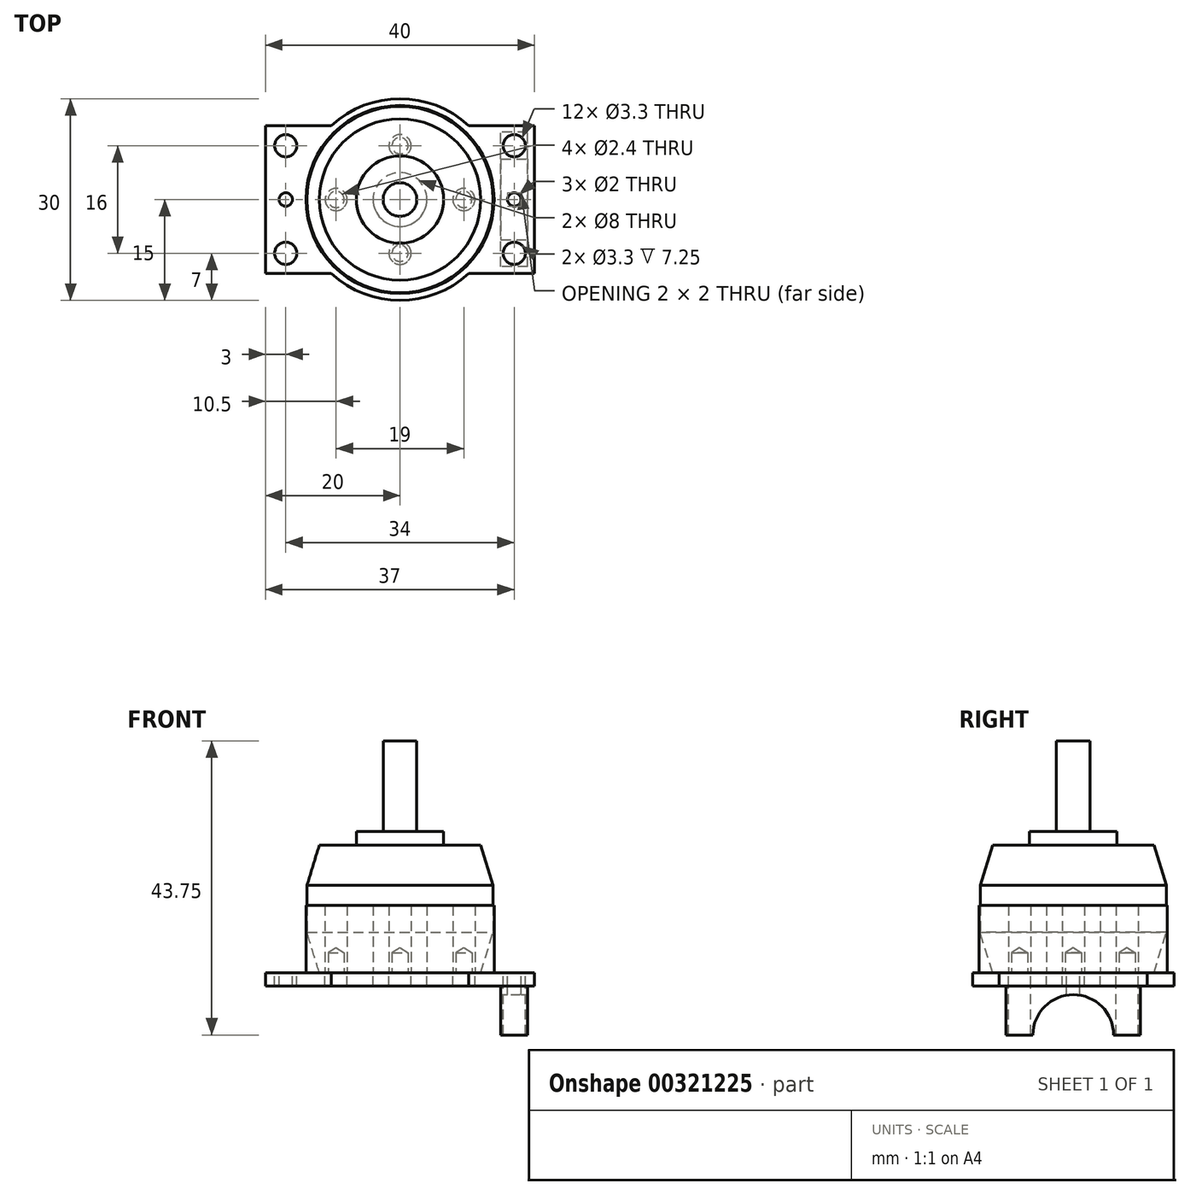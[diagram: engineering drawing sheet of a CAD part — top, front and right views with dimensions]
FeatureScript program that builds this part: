
annotation { "Feature Type Name" : "Feature", "Feature Type Description" : "" }
export const myFeature = defineFeature(function(context is Context, id is Id, definition is map)
    precondition{}
    {
        {
            var Q0;
            Q0=qCreatedBy(makeId("Front.planeOp"),FACE);
            var sketch = newSketch(context, id + "F0", { "sketchPlane" : qUnion([Q0])});
            skLineSegment(sketch, "E0", {"start": v(0, 0) * mm, "end": v(0, 34.5) * mm});
            skLineSegment(sketch, "E1", {"start": v(-6.5, 21) * mm, "end": v(-6.5, 19) * mm});
            skLineSegment(sketch, "E2", {"start": v(-13.85, 13) * mm, "end": v(-13.85, 6) * mm});
            skLineSegment(sketch, "E3", {"start": v(-13.85, 6) * mm, "end": v(-12, 0) * mm});
            skLineSegment(sketch, "E4", {"start": v(-12, 0) * mm, "end": v(0, 0) * mm});
            skLineSegment(sketch, "E5", {"start": v(-6.5, 19) * mm, "end": v(-12, 19) * mm});
            skLineSegment(sketch, "E6", {"start": v(-12, 19) * mm, "end": v(-13.85, 13) * mm});
            skLineSegment(sketch, "E7", {"start": v(-6.5, 21) * mm, "end": v(-2.5, 21) * mm});
            skLineSegment(sketch, "E8", {"start": v(-2.5, 21) * mm, "end": v(-2.5, 34.5) * mm});
            skLineSegment(sketch, "E9", {"start": v(-2.5, 34.5) * mm, "end": v(0, 34.5) * mm});
            skSolve(sketch);
        }
        {
            var Q0;
            Q0 = qSketchRegion(id + "F0", true);
            var Q1;
            Q1=sQuery(id+"F0.wireOp",EDGE,"E0");
            revolve(context, id + "F1", {"entities" : qUnion([Q0]), "axis" : qUnion([Q1]), "revolveType" : RevolveType.FULL});
        }
        {
            var Q0;
            Q0=makeQuery(id+"F1.opRevolve","SWEPT_FACE",FACE,{"disambiguationData":[OSD([sQuery(id+"F0.wireOp",EDGE,"E4")])]});
            var sketch = newSketch(context, id + "F2", { "sketchPlane" : qUnion([Q0])});
            skCircle(sketch, "E10", {"center": v(0, 0) * mm, "radius": 8 * mm, "construction": true});
            skCircle(sketch, "E11", {"center": v(0, 0) * mm, "radius": 9.5 * mm, "construction": true});
            skPoint(sketch, "E12", {"position": v(0, 8) * mm});
            skPoint(sketch, "E13", {"position": v(0, -8) * mm});
            skPoint(sketch, "E14", {"position": v(9.5, 0) * mm});
            skPoint(sketch, "E15", {"position": v(-9.5, 0) * mm});
            skSolve(sketch);
        }
        {
            var Q0;
            Q0=sQuery(id+"F2.wireOp",VERTEX,"E12");
            var Q1;
            Q1=sQuery(id+"F2.wireOp",VERTEX,"E15");
            var Q2;
            Q2=sQuery(id+"F2.wireOp",VERTEX,"E13");
            var Q3;
            Q3=sQuery(id+"F2.wireOp",VERTEX,"E14");
            var Q4;
            Q4=makeQuery(id+"F1.opRevolve","SWEPT_BODY",BODY,{"disambiguationData":[OSD([sQuery(id+"F0.wireOp",EDGE,"E0"),sQuery(id+"F0.wireOp",EDGE,"E1"),sQuery(id+"F0.wireOp",EDGE,"E2"),sQuery(id+"F0.wireOp",EDGE,"E3"),sQuery(id+"F0.wireOp",EDGE,"E4"),sQuery(id+"F0.wireOp",EDGE,"E5"),sQuery(id+"F0.wireOp",EDGE,"E6"),sQuery(id+"F0.wireOp",EDGE,"E7"),sQuery(id+"F0.wireOp",EDGE,"E8"),sQuery(id+"F0.wireOp",EDGE,"E9")])]});
            hole(context, id + "F3", {"style" : HoleStyle.SIMPLE, "endStyle" : HoleEndStyle.BLIND, "standardTappedOrClearance" : lookupTablePath({ "standard" : "ISO", "engagement" : "75%", "pitch" : "0.6 mm", "size" : "M3", "type" : "Tapped" }), "standardBlindInLast" : lookupTablePath({ "standard" : "ISO", "engagement" : "75%", "pitch" : "0.6 mm", "size" : "M3", "type" : "Tapped" }), "holeDiameter" : 2.4 * mm, "showTappedDepth" : true, "holeDepth" : 3 * mm, "tappedDepth" : 1.2 * mm, "tapClearance" : 3, "locations" : qUnion([Q0, Q1, Q2, Q3]), "scope" : qUnion([Q4])});
        }
        {
            var Q0;
            Q0=makeQuery(id+"F1.opRevolve","SWEPT_FACE",FACE,{"disambiguationData":[OSD([sQuery(id+"F0.wireOp",EDGE,"E4")])]});
            var sketch = newSketch(context, id + "F4", { "sketchPlane" : qUnion([Q0])});
            skLineSegment(sketch, "E16.bottom", {"start": v(20, -11) * mm, "end": v(-20, -11) * mm});
            skLineSegment(sketch, "E16.top", {"start": v(20, 11) * mm, "end": v(-20, 11) * mm});
            skLineSegment(sketch, "E16.left", {"start": v(20, -11) * mm, "end": v(20, 11) * mm});
            skLineSegment(sketch, "E16.right", {"start": v(-20, -11) * mm, "end": v(-20, 11) * mm});
            skPoint(sketch, "E16.middle", {"position": v(0, 0) * mm});
            skCircle(sketch, "E17", {"center": v(0, 0) * mm, "radius": 15 * mm});
            skLineSegment(sketch, "E18.bottom", {"start": v(17, -8) * mm, "end": v(-17, -8) * mm, "construction": true});
            skLineSegment(sketch, "E18.top", {"start": v(17, 8) * mm, "end": v(-17, 8) * mm, "construction": true});
            skLineSegment(sketch, "E18.left", {"start": v(17, -8) * mm, "end": v(17, 8) * mm, "construction": true});
            skLineSegment(sketch, "E18.right", {"start": v(-17, -8) * mm, "end": v(-17, 8) * mm, "construction": true});
            skPoint(sketch, "E19", {"position": v(-17, 0) * mm});
            skPoint(sketch, "E20", {"position": v(17, 0) * mm});
            skSolve(sketch);
        }
        {
            var Q0;
            Q0 = qSketchRegion(id + "F4", true);
            extrude(context, id + "F5", {"entities" : qUnion([Q0]), "depth" : 2 * mm});
        }
        {
            var Q0;
            Q0=sQuery(id+"F2.wireOp",VERTEX,"E12");
            var Q1;
            Q1=sQuery(id+"F2.wireOp",VERTEX,"E15");
            var Q2;
            Q2=sQuery(id+"F2.wireOp",VERTEX,"E14");
            var Q3;
            Q3=sQuery(id+"F2.wireOp",VERTEX,"E13");
            var Q4;
            Q4=sQuery(id+"F4.wireOp",VERTEX,"E18.top.end");
            var Q5;
            Q5=sQuery(id+"F4.wireOp",VERTEX,"E18.top.start");
            var Q6;
            Q6=sQuery(id+"F4.wireOp",VERTEX,"E18.bottom.end");
            var Q7;
            Q7=sQuery(id+"F4.wireOp",VERTEX,"E18.left.start");
            var Q8;
            Q8=makeQuery(id+"F5.opExtrude","SWEPT_BODY",BODY,{"disambiguationData":[OSD([sQuery(id+"F4.wireOp",EDGE,"E16.bottom"),sQuery(id+"F4.wireOp",EDGE,"E16.top"),sQuery(id+"F4.wireOp",EDGE,"E16.left"),sQuery(id+"F4.wireOp",EDGE,"E16.right"),sQuery(id+"F4.wireOp",EDGE,"E17")])]});
            hole(context, id + "F6", {"style" : HoleStyle.SIMPLE, "endStyle" : HoleEndStyle.THROUGH, "oppositeDirection" : true, "standardTappedOrClearance" : lookupTablePath({ "standard" : "ISO", "fit" : "Normal", "size" : "M3", "type" : "Clearance" }), "standardBlindInLast" : lookupTablePath({ "fit" : "Standard", "standard" : "ISO", "size" : "M3", "type" : "Clearance" }), "holeDiameter" : 3.3 * mm, "tappedDepth" : 1.2 * mm, "tapClearance" : 3, "locations" : qUnion([Q0, Q1, Q2, Q3, Q4, Q5, Q6, Q7]), "scope" : qUnion([Q8])});
        }
        {
            var Q0;
            Q0=sQuery(id+"F4.wireOp",VERTEX,"E19");
            var Q1;
            Q1=sQuery(id+"F4.wireOp",VERTEX,"E20");
            var Q2;
            Q2=makeQuery(id+"F5.opExtrude","SWEPT_BODY",BODY,{"disambiguationData":[OSD([sQuery(id+"F4.wireOp",EDGE,"E16.bottom"),sQuery(id+"F4.wireOp",EDGE,"E16.top"),sQuery(id+"F4.wireOp",EDGE,"E16.left"),sQuery(id+"F4.wireOp",EDGE,"E16.right"),sQuery(id+"F4.wireOp",EDGE,"E17")])]});
            hole(context, id + "F7", {"style" : HoleStyle.SIMPLE, "endStyle" : HoleEndStyle.THROUGH, "oppositeDirection" : true, "holeDiameter" : 2 * mm, "tappedDepth" : 1.2 * mm, "tapClearance" : 3, "locations" : qUnion([Q0, Q1]), "scope" : qUnion([Q2])});
        }
        {
            var Q0;
            Q0=sQuery(id+"F4.wireOp",VERTEX,"E16.middle");
            var Q1;
            Q1=makeQuery(id+"F5.opExtrude","SWEPT_BODY",BODY,{"disambiguationData":[OSD([sQuery(id+"F4.wireOp",EDGE,"E16.bottom"),sQuery(id+"F4.wireOp",EDGE,"E16.top"),sQuery(id+"F4.wireOp",EDGE,"E16.left"),sQuery(id+"F4.wireOp",EDGE,"E16.right"),sQuery(id+"F4.wireOp",EDGE,"E17")])]});
            hole(context, id + "F8", {"style" : HoleStyle.SIMPLE, "endStyle" : HoleEndStyle.THROUGH, "oppositeDirection" : true, "holeDiameter" : 8 * mm, "isTappedThrough" : true, "tappedDepth" : 1.2 * mm, "tapClearance" : 3, "locations" : qUnion([Q0]), "scope" : qUnion([Q1])});
        }
        {
            var Q0;
            Q0=makeQuery(id+"F5.opExtrude","CAP_FACE",FACE,{"disambiguationData":[OSD([sQuery(id+"F4.wireOp",EDGE,"E16.bottom"),sQuery(id+"F4.wireOp",EDGE,"E16.top"),sQuery(id+"F4.wireOp",EDGE,"E16.left"),sQuery(id+"F4.wireOp",EDGE,"E16.right"),sQuery(id+"F4.wireOp",EDGE,"E17")])],"isStart":false});
            var sketch = newSketch(context, id + "F9", { "sketchPlane" : qUnion([Q0])});
            skLineSegment(sketch, "E21.bottom", {"start": v(19, 10) * mm, "end": v(15, 10) * mm});
            skLineSegment(sketch, "E21.top", {"start": v(19, -10) * mm, "end": v(15, -10) * mm});
            skLineSegment(sketch, "E21.left", {"start": v(19, 10) * mm, "end": v(19, -10) * mm});
            skLineSegment(sketch, "E21.right", {"start": v(15, 10) * mm, "end": v(15, -10) * mm});
            skPoint(sketch, "E21.middle", {"position": v(17, 0) * mm});
            skSolve(sketch);
        }
        {
            var Q0;
            Q0=makeQuery(id+"F9.imprint","IMPRINT",FACE,{"disambiguationData":[TD([[makeQuery(id+"F9.imprint","IMPRINT",EDGE,{"derivedFrom":sQuery(id+"F9.wireOp",EDGE,"E21.bottom")}),1.0]])]});
            extrude(context, id + "F10", {"entities" : qUnion([Q0]), "depth" : 7.25 * mm});
        }
        {
            var Q0;
            Q0=makeQuery(id+"F10.opExtrude","SWEPT_FACE",FACE,{"disambiguationData":[OSD([sQuery(id+"F9.wireOp",EDGE,"E21.left")])]});
            var sketch = newSketch(context, id + "F11", { "sketchPlane" : qUnion([Q0])});
            skCircle(sketch, "E22", {"center": v(0, -9.25) * mm, "radius": 6 * mm});
            skSolve(sketch);
        }
        {
            var Q0;
            Q0 = qSketchRegion(id + "F11", true);
            extrude(context, id + "F12", {"entities" : qUnion([Q0]), "operationType" : NewBodyOperationType.REMOVE, "oppositeDirection" : true, "depth" : 25 * mm});
        }
        {
            var Q0;
            Q0=makeQuery(id+"F5.opExtrude","CAP_FACE",FACE,{"disambiguationData":[OSD([sQuery(id+"F4.wireOp",EDGE,"E16.bottom"),sQuery(id+"F4.wireOp",EDGE,"E16.top"),sQuery(id+"F4.wireOp",EDGE,"E16.left"),sQuery(id+"F4.wireOp",EDGE,"E16.right"),sQuery(id+"F4.wireOp",EDGE,"E17")])],"isStart":true});
            var sketch = newSketch(context, id + "F13", { "sketchPlane" : qUnion([Q0])});
            skCircle(sketch, "E23", {"center": v(0, 0) * mm, "radius": 14 * mm});
            skSolve(sketch);
        }
        {
            var Q0;
            Q0=makeQuery(id+"F13.imprint","IMPRINT",FACE,{"disambiguationData":[TD([[makeQuery(id+"F13.imprint","IMPRINT",EDGE,{"derivedFrom":sQuery(id+"F13.wireOp",EDGE,"E23")}),1.0]])]});
            extrude(context, id + "F14", {"entities" : qUnion([Q0]), "depth" : 10 * mm});
        }
    });
